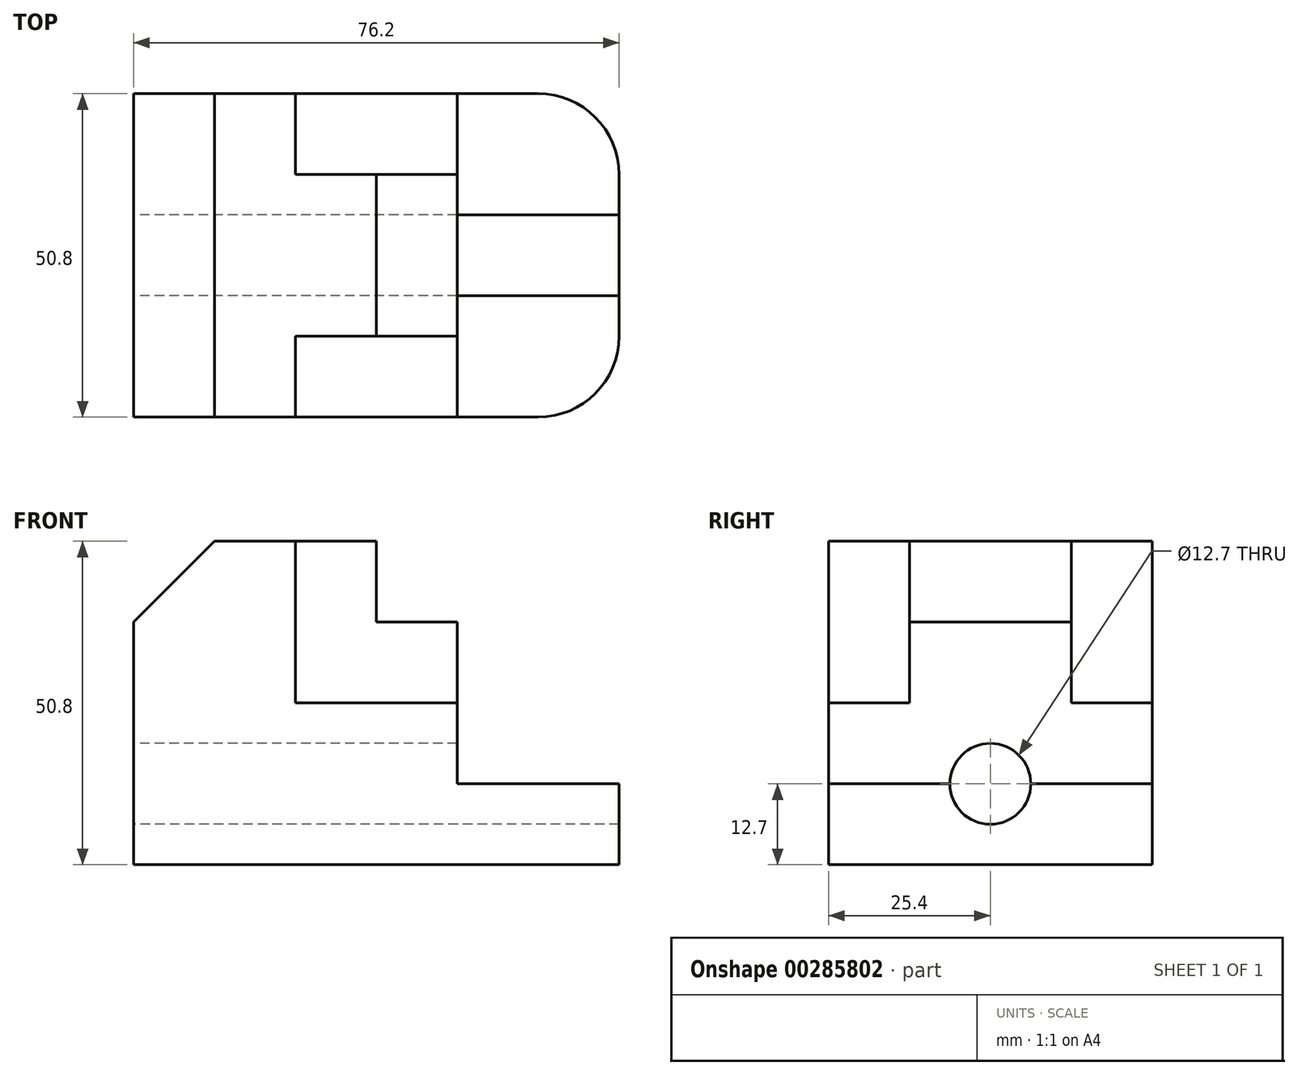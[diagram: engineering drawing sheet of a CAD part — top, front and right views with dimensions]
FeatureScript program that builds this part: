
annotation { "Feature Type Name" : "Feature", "Feature Type Description" : "" }
export const myFeature = defineFeature(function(context is Context, id is Id, definition is map)
    precondition{}
    {
        {
            var Q0;
            Q0=qCreatedBy(makeId("Front.planeOp"),FACE);
            var sketch = newSketch(context, id + "F0", { "sketchPlane" : qUnion([Q0])});
            skLineSegment(sketch, "E0", {"start": v(-38.1, 0) * mm, "end": v(-38.1, 38.1) * mm});
            skLineSegment(sketch, "E1", {"start": v(-38.1, 38.1) * mm, "end": v(-25.4, 50.8) * mm});
            skLineSegment(sketch, "E2", {"start": v(-25.4, 50.8) * mm, "end": v(0, 50.8) * mm});
            skLineSegment(sketch, "E3", {"start": v(0, 50.8) * mm, "end": v(0, 38.1) * mm});
            skLineSegment(sketch, "E4", {"start": v(0, 38.1) * mm, "end": v(12.7, 38.1) * mm});
            skLineSegment(sketch, "E5", {"start": v(12.7, 38.1) * mm, "end": v(12.7, 12.7) * mm});
            skLineSegment(sketch, "E6", {"start": v(12.7, 12.7) * mm, "end": v(38.1, 12.7) * mm});
            skLineSegment(sketch, "E7", {"start": v(38.1, 12.7) * mm, "end": v(38.1, 0) * mm});
            skLineSegment(sketch, "E8", {"start": v(38.1, 0) * mm, "end": v(-38.1, 0) * mm});
            skLineSegment(sketch, "E9", {"start": v(-12.7, 50.8) * mm, "end": v(-12.7, 25.4) * mm});
            skLineSegment(sketch, "E10", {"start": v(-12.7, 25.4) * mm, "end": v(12.7, 25.4) * mm});
            skSolve(sketch);
        }
        {
            var Q0;
            Q0=makeQuery(id+"F0.imprint","IMPRINT",FACE,{"disambiguationData":[TD([[makeQuery(id+"F0.imprint","IMPRINT",EDGE,{"derivedFrom":sQuery(id+"F0.wireOp",EDGE,"E0")}),-1.0]])]});
            var Q1;
            {var subQ3=sQuery(id+"F0.wireOp",EDGE,"E3");Q1=makeQuery(id+"F0.imprint","IMPRINT",FACE,{"disambiguationData":[TD([[makeQuery(id+"F0.imprint","IMPRINT",EDGE,{"derivedFrom":subQ3}),-1.0]])]});}
            extrude(context, id + "F1", {"entities" : qUnion([Q0, Q1]), "depth" : 50.8 * mm, "symmetric" : true});
        }
        {
            var Q0;
            Q0=makeQuery(id+"F1.opExtrude","SWEPT_FACE",FACE,{"disambiguationData":[OSD([sQuery(id+"F0.wireOp",EDGE,"E2")])]});
            var sketch = newSketch(context, id + "F2", { "sketchPlane" : qUnion([Q0])});
            skLineSegment(sketch, "E11", {"start": v(-12.7, 25.4) * mm, "end": v(-12.7, 12.7) * mm});
            skLineSegment(sketch, "E12", {"start": v(-12.7, 12.7) * mm, "end": v(12.7, 12.7) * mm});
            skLineSegment(sketch, "E13", {"start": v(-12.7, -25.4) * mm, "end": v(-12.7, -12.7) * mm});
            skLineSegment(sketch, "E14", {"start": v(-12.7, -12.7) * mm, "end": v(12.7, -12.7) * mm});
            skLineSegment(sketch, "E15", {"start": v(12.7, -12.7) * mm, "end": v(12.7, -25.4) * mm});
            skLineSegment(sketch, "E16", {"start": v(12.7, -25.4) * mm, "end": v(-12.7, -25.4) * mm});
            skLineSegment(sketch, "E17", {"start": v(-12.7, 25.4) * mm, "end": v(12.7, 25.4) * mm});
            skLineSegment(sketch, "E18", {"start": v(12.7, 25.4) * mm, "end": v(12.7, 12.7) * mm});
            skSolve(sketch);
        }
        {
            var Q0;
            {var subQ0=sQuery(id+"F2.wireOp",EDGE,"E15");Q0=makeQuery(id+"F2.imprint","IMPRINT",FACE,{"disambiguationData":[TD([[makeQuery(id+"F2.imprint","IMPRINT",EDGE,{"derivedFrom":subQ0}),-1.0]])]});}
            var Q1;
            {var subQ0=sQuery(id+"F2.wireOp",EDGE,"E13");Q1=makeQuery(id+"F2.imprint","IMPRINT",FACE,{"disambiguationData":[TD([[makeQuery(id+"F2.imprint","IMPRINT",EDGE,{"derivedFrom":subQ0}),-1.0]])]});}
            var Q2;
            {var subQ0=sQuery(id+"F2.wireOp",EDGE,"E18");Q2=makeQuery(id+"F2.imprint","IMPRINT",FACE,{"disambiguationData":[TD([[makeQuery(id+"F2.imprint","IMPRINT",EDGE,{"derivedFrom":subQ0}),-1.0]])]});}
            var Q3;
            {var subQ0=sQuery(id+"F2.wireOp",EDGE,"E11");Q3=makeQuery(id+"F2.imprint","IMPRINT",FACE,{"disambiguationData":[TD([[makeQuery(id+"F2.imprint","IMPRINT",EDGE,{"derivedFrom":subQ0}),1.0]])]});}
            extrude(context, id + "F3", {"entities" : qUnion([Q0, Q1, Q2, Q3]), "operationType" : NewBodyOperationType.REMOVE, "oppositeDirection" : true, "depth" : 25.4 * mm});
        }
        {
            var Q0;
            Q0=makeQuery(id+"F1.opExtrude","SWEPT_FACE",FACE,{"disambiguationData":[OSD([sQuery(id+"F0.wireOp",EDGE,"E5")])]});
            var sketch = newSketch(context, id + "F4", { "sketchPlane" : qUnion([Q0])});
            skCircle(sketch, "E19", {"center": v(0, 12.7) * mm, "radius": 6.35 * mm});
            skSolve(sketch);
        }
        {
            var Q0;
            {var subQ0=sQuery(id+"F4.wireOp",EDGE,"E19");var subQ1=makeQuery(id+"F1.opExtrude","SWEPT_EDGE",EDGE,{"disambiguationData":[OSD([sQuery(id+"F0.wireOp",EDGE,"E5"),sQuery(id+"F0.wireOp",EDGE,"E6")])]});var subQ2=makeQuery(id+"F4.imprint","INTERSECT",VERTEX,{"disambiguationData":[OD(0.0)],"derivedFrom":[subQ1,subQ0]});Q0=makeQuery(id+"F4.imprint","IMPRINT",FACE,{"disambiguationData":[TD([[makeQuery(id+"F4.imprint","IMPRINT",EDGE,{"disambiguationData":[TD([[subQ2,-1.0]])],"derivedFrom":subQ0}),1.0]])]});}
            var Q1;
            {var subQ0=sQuery(id+"F4.wireOp",EDGE,"E19");var subQ1=makeQuery(id+"F1.opExtrude","SWEPT_EDGE",EDGE,{"disambiguationData":[OSD([sQuery(id+"F0.wireOp",EDGE,"E5"),sQuery(id+"F0.wireOp",EDGE,"E6")])]});var subQ2=makeQuery(id+"F4.imprint","INTERSECT",VERTEX,{"disambiguationData":[OD(0.0)],"derivedFrom":[subQ1,subQ0]});Q1=makeQuery(id+"F4.imprint","IMPRINT",FACE,{"disambiguationData":[TD([[makeQuery(id+"F4.imprint","IMPRINT",EDGE,{"disambiguationData":[TD([[subQ2,1.0]])],"derivedFrom":subQ0}),1.0]])]});}
            extrude(context, id + "F5", {"entities" : qUnion([Q0, Q1]), "operationType" : NewBodyOperationType.REMOVE, "endBound" : BoundingType.THROUGH_ALL, "depth" : 25.4 * mm, "hasSecondDirection" : true, "secondDirectionBound" : BoundingType.THROUGH_ALL, "secondDirectionOppositeDirection" : true, "secondDirectionDepth" : 25.4 * mm});
        }
        {
            var Q0;
            {var subQ0=sQuery(id+"F0.wireOp",EDGE,"E7");var subQ1=sQuery(id+"F0.wireOp",EDGE,"E6");var subQ2=sQuery(id+"F0.wireOp",EDGE,"E5");Q0=makeQuery(id+"F5.boolean.opBoolean","SPLIT",FACE,{"disambiguationData":[TD([makeQuery(id+"F1.opExtrude","CAP_FACE",FACE,{"disambiguationData":[OSD([sQuery(id+"F0.wireOp",EDGE,"E0"),sQuery(id+"F0.wireOp",EDGE,"E1"),sQuery(id+"F0.wireOp",EDGE,"E2"),sQuery(id+"F0.wireOp",EDGE,"E3"),sQuery(id+"F0.wireOp",EDGE,"E4"),subQ2,subQ1,subQ0,sQuery(id+"F0.wireOp",EDGE,"E8")])],"isStart":true})])],"derivedFrom":makeQuery(id+"F1.opExtrude","SWEPT_FACE",FACE,{"disambiguationData":[OSD([subQ1])]})});}
            var sketch = newSketch(context, id + "F6", { "sketchPlane" : qUnion([Q0])});
            skArc(sketch, "E20", {"start": v(38.1, 12.7) * mm, "mid": v(34.38, 21.68) * mm, "end": v(25.4, 25.4) * mm});
            skLineSegment(sketch, "E21", {"start": v(38.1, 12.7) * mm, "end": v(38.1, 6.35) * mm});
            skLineSegment(sketch, "E22", {"start": v(38.1, 12.7) * mm, "end": v(38.1, 25.4) * mm});
            skLineSegment(sketch, "E23", {"start": v(38.1, 25.4) * mm, "end": v(25.4, 25.4) * mm});
            skSolve(sketch);
        }
        {
            var Q0;
            Q0=makeQuery(id+"F6.imprint","IMPRINT",FACE,{"disambiguationData":[TD([[makeQuery(id+"F6.imprint","IMPRINT",EDGE,{"derivedFrom":sQuery(id+"F6.wireOp",EDGE,"E20")}),-1.0]])]});
            extrude(context, id + "F7", {"entities" : qUnion([Q0]), "operationType" : NewBodyOperationType.REMOVE, "endBound" : BoundingType.THROUGH_ALL, "oppositeDirection" : true, "depth" : 25.4 * mm});
        }
        {
            var Q0;
            {var subQ0=sQuery(id+"F0.wireOp",EDGE,"E7");var subQ1=sQuery(id+"F0.wireOp",EDGE,"E6");var subQ2=sQuery(id+"F0.wireOp",EDGE,"E5");Q0=makeQuery(id+"F5.boolean.opBoolean","SPLIT",FACE,{"disambiguationData":[TD([makeQuery(id+"F1.opExtrude","CAP_FACE",FACE,{"disambiguationData":[OSD([sQuery(id+"F0.wireOp",EDGE,"E0"),sQuery(id+"F0.wireOp",EDGE,"E1"),sQuery(id+"F0.wireOp",EDGE,"E2"),sQuery(id+"F0.wireOp",EDGE,"E3"),sQuery(id+"F0.wireOp",EDGE,"E4"),subQ2,subQ1,subQ0,sQuery(id+"F0.wireOp",EDGE,"E8")])],"isStart":false})])],"derivedFrom":makeQuery(id+"F1.opExtrude","SWEPT_FACE",FACE,{"disambiguationData":[OSD([subQ1])]})});}
            var sketch = newSketch(context, id + "F8", { "sketchPlane" : qUnion([Q0])});
            skLineSegment(sketch, "E24", {"start": v(38.1, -6.35) * mm, "end": v(38.1, -25.4) * mm});
            skLineSegment(sketch, "E25", {"start": v(38.1, -25.4) * mm, "end": v(25.4, -25.4) * mm});
            skLineSegment(sketch, "E26", {"start": v(38.1, -6.35) * mm, "end": v(38.1, -12.7) * mm});
            skArc(sketch, "E27", {"start": v(25.4, -25.4) * mm, "mid": v(34.38, -21.68) * mm, "end": v(38.1, -12.7) * mm});
            skSolve(sketch);
        }
        {
            var Q0;
            Q0=makeQuery(id+"F8.imprint","IMPRINT",FACE,{"disambiguationData":[TD([[makeQuery(id+"F8.imprint","IMPRINT",EDGE,{"derivedFrom":sQuery(id+"F8.wireOp",EDGE,"E24")}),1.0]])]});
            extrude(context, id + "F9", {"entities" : qUnion([Q0]), "operationType" : NewBodyOperationType.REMOVE, "endBound" : BoundingType.THROUGH_ALL, "oppositeDirection" : true, "depth" : 25.4 * mm});
        }
    });
